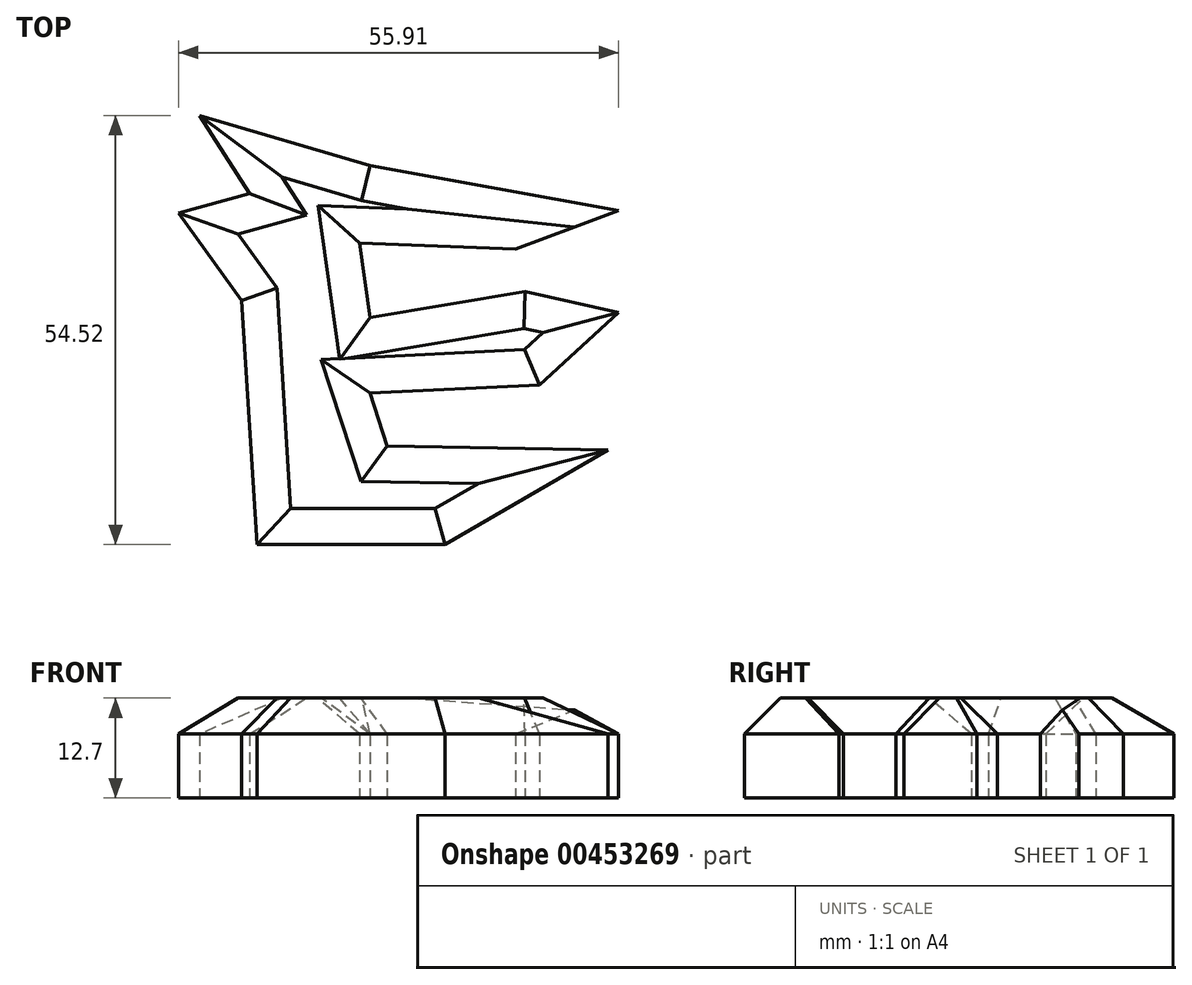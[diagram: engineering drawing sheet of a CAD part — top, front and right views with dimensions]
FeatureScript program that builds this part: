
annotation { "Feature Type Name" : "Feature", "Feature Type Description" : "" }
export const myFeature = defineFeature(function(context is Context, id is Id, definition is map)
    precondition{}
    {
        {
            var Q0;
            Q0=qCreatedBy(makeId("Top.planeOp"),FACE);
            var sketch = newSketch(context, id + "F0", { "sketchPlane" : qUnion([Q0])});
            skLineSegment(sketch, "E0", {"start": v(6.21, 57.34) * mm, "end": v(27.87, 50.96) * mm});
            skLineSegment(sketch, "E1", {"start": v(27.87, 50.96) * mm, "end": v(59.44, 45.27) * mm});
            skLineSegment(sketch, "E2", {"start": v(59.44, 45.27) * mm, "end": v(46.34, 40.38) * mm});
            skLineSegment(sketch, "E3", {"start": v(46.34, 40.38) * mm, "end": v(26.54, 41.1) * mm});
            skLineSegment(sketch, "E4", {"start": v(26.54, 41.1) * mm, "end": v(27.87, 31.65) * mm});
            skLineSegment(sketch, "E5", {"start": v(27.87, 31.65) * mm, "end": v(47.55, 34.94) * mm});
            skLineSegment(sketch, "E6", {"start": v(47.55, 34.94) * mm, "end": v(59.44, 32.32) * mm});
            skLineSegment(sketch, "E7", {"start": v(59.44, 32.32) * mm, "end": v(49.37, 23.09) * mm});
            skLineSegment(sketch, "E8", {"start": v(49.37, 23.09) * mm, "end": v(27.87, 22.06) * mm});
            skLineSegment(sketch, "E9", {"start": v(27.87, 22.06) * mm, "end": v(30.06, 15.36) * mm});
            skLineSegment(sketch, "E10", {"start": v(30.06, 15.36) * mm, "end": v(58.1, 14.83) * mm});
            skLineSegment(sketch, "E11", {"start": v(58.1, 14.83) * mm, "end": v(37.38, 2.82) * mm});
            skLineSegment(sketch, "E12", {"start": v(37.38, 2.82) * mm, "end": v(13.5, 2.87) * mm});
            skLineSegment(sketch, "E13", {"start": v(6.21, 57.34) * mm, "end": v(12.6, 47.44) * mm});
            skLineSegment(sketch, "E14", {"start": v(12.6, 47.44) * mm, "end": v(3.53, 44.92) * mm});
            skLineSegment(sketch, "E15", {"start": v(13.5, 2.87) * mm, "end": v(11.56, 33.82) * mm});
            skLineSegment(sketch, "E16", {"start": v(11.56, 33.82) * mm, "end": v(3.53, 44.92) * mm});
            skSolve(sketch);
        }
        {
            var Q0;
            Q0=qSketchRegion(id+"F0",true);
            var Q1;
            Q1=qSketchRegion(id+"FhSuuO6UR1XzC2C_4",true);
            var Q2;
            Q2=qSketchRegion(id+"FTeMgZZDWwlIoI5_4",true);
            var Q3;
            Q3=qSketchRegion(id+"FiezEiqxvGsPzSm_4",true);
            extrude(context, id + "F1", {"entities" : qUnion([Q0, Q1, Q2, Q3]), "depth" : 12.7 * mm});
        }
        {
            var Q0;
            Q0=makeQuery(id+"F1.opExtrude","CAP_FACE",FACE,{"disambiguationData":[OSD([sQuery(id+"F0.wireOp",EDGE,"E0"),sQuery(id+"F0.wireOp",EDGE,"E1"),sQuery(id+"F0.wireOp",EDGE,"E2"),sQuery(id+"F0.wireOp",EDGE,"E3"),sQuery(id+"F0.wireOp",EDGE,"E4"),sQuery(id+"F0.wireOp",EDGE,"E5"),sQuery(id+"F0.wireOp",EDGE,"E6"),sQuery(id+"F0.wireOp",EDGE,"E7"),sQuery(id+"F0.wireOp",EDGE,"E8"),sQuery(id+"F0.wireOp",EDGE,"E9"),sQuery(id+"F0.wireOp",EDGE,"E10"),sQuery(id+"F0.wireOp",EDGE,"E11"),sQuery(id+"F0.wireOp",EDGE,"E12"),sQuery(id+"F0.wireOp",EDGE,"E13"),sQuery(id+"F0.wireOp",EDGE,"E14"),sQuery(id+"F0.wireOp",EDGE,"973260f2-bf32-4142-aa3f-1c42aafbad0a")])],"isStart":false});
            chamfer(context, id + "F2", {"entities" : qUnion([Q0]), "width" : 4.57 * mm, "tangentPropagation" : true});
        }
    });
